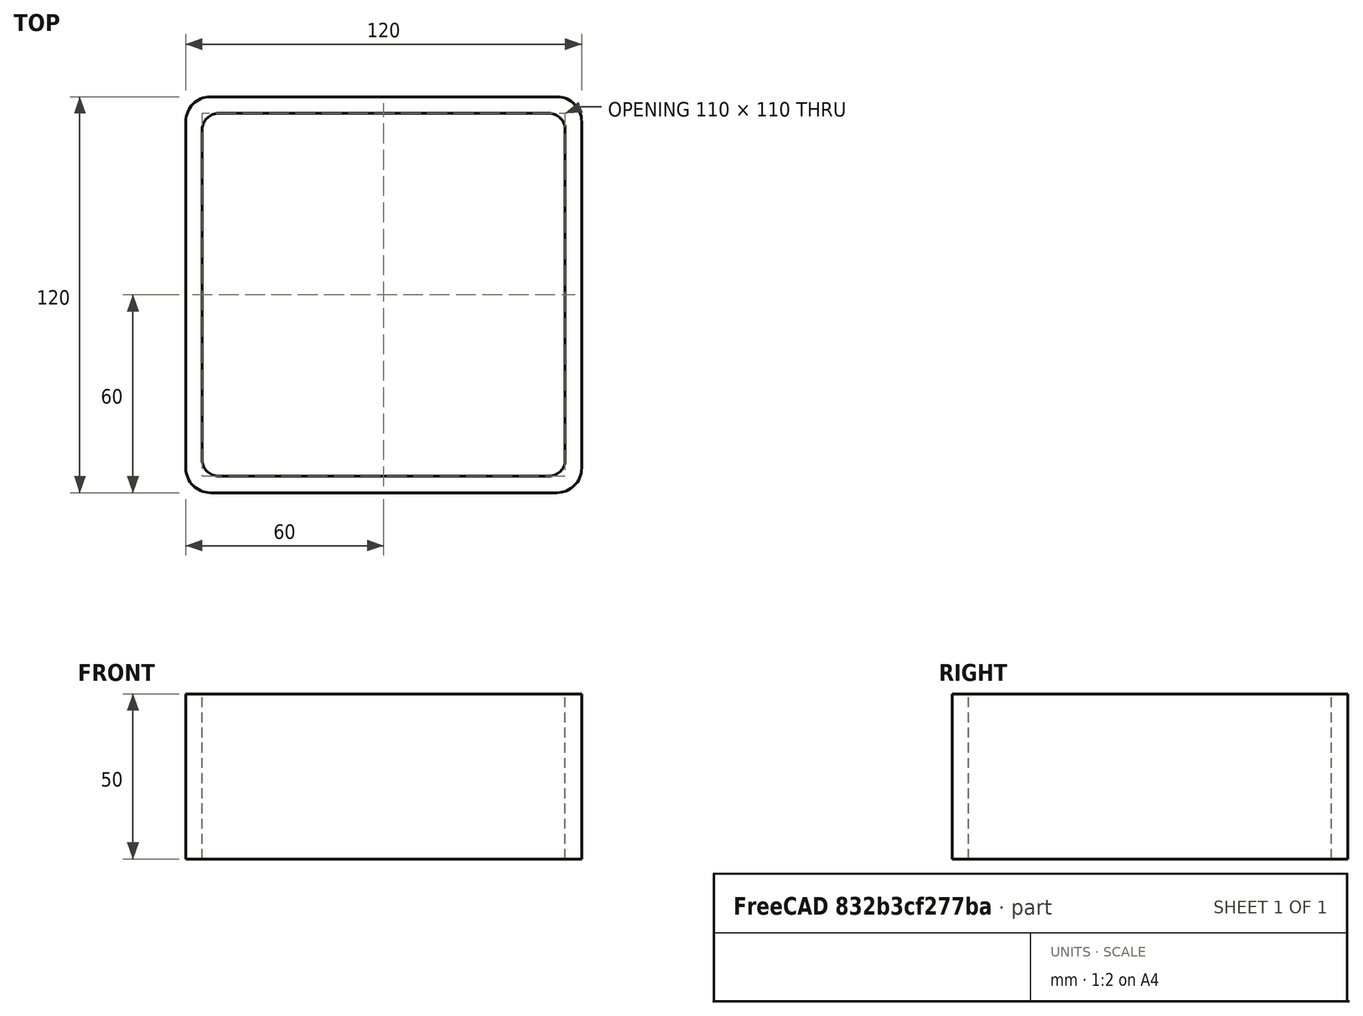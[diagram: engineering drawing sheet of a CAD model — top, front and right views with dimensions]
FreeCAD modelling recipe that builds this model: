
FCSTD DOCUMENT  (FreeCAD 0.15R4671 (Git))
Label: Square hollow section 120x120x5 EN10219 S235JRH
License: All rights reserved
LicenseURL: http://en.wikipedia.org/wiki/All_rights_reserved
objects: Sketcher::SketchObject×1, Part::Extrusion×1
note: 2 computed .brp shape members not serialized (recipe doc carries the construction recipe); baked Part::Feature solids carry a one-line shape summary decoded from their .brp

FEATURE [Sketcher::SketchObject] Sketch
  sketch-geometry (16):
    g0: LineSegment StartX=-50 StartY=55 StartZ=0 EndX=50 EndY=55 EndZ=0
    g1: LineSegment StartX=55 StartY=50 StartZ=0 EndX=55 EndY=-50 EndZ=0
    g2: LineSegment StartX=50 StartY=-55 StartZ=0 EndX=-50 EndY=-55 EndZ=0
    g3: LineSegment StartX=-55 StartY=-50 StartZ=0 EndX=-55 EndY=50 EndZ=0
    g4: LineSegment StartX=-52.5 StartY=60 StartZ=0 EndX=52.5 EndY=60 EndZ=0
    g5: LineSegment StartX=60 StartY=52.5 StartZ=0 EndX=60 EndY=-52.5 EndZ=0
    g6: LineSegment StartX=52.5 StartY=-60 StartZ=0 EndX=-52.5 EndY=-60 EndZ=0
    g7: LineSegment StartX=-60 StartY=-52.5 StartZ=0 EndX=-60 EndY=52.5 EndZ=0
    g8: ArcOfCircle CenterX=-50 CenterY=50 CenterZ=0 NormalX=0 NormalY=0 NormalZ=1 Radius=5 StartAngle=1.5708 EndAngle=3.14159
    g9: ArcOfCircle CenterX=50 CenterY=50 CenterZ=0 NormalX=0 NormalY=0 NormalZ=1 Radius=5 StartAngle=0 EndAngle=1.5708
    g10: ArcOfCircle CenterX=50 CenterY=-50 CenterZ=0 NormalX=0 NormalY=0 NormalZ=1 Radius=5 StartAngle=4.71239 EndAngle=6.28319
    g11: ArcOfCircle CenterX=-50 CenterY=-50 CenterZ=0 NormalX=0 NormalY=0 NormalZ=1 Radius=5 StartAngle=3.14159 EndAngle=4.71239
    g12: ArcOfCircle CenterX=52.5 CenterY=52.5 CenterZ=0 NormalX=0 NormalY=0 NormalZ=1 Radius=7.5 StartAngle=0 EndAngle=1.5708
    g13: ArcOfCircle CenterX=52.5 CenterY=-52.5 CenterZ=0 NormalX=0 NormalY=0 NormalZ=1 Radius=7.5 StartAngle=4.71239 EndAngle=6.28319
    g14: ArcOfCircle CenterX=-52.5 CenterY=-52.5 CenterZ=0 NormalX=0 NormalY=0 NormalZ=1 Radius=7.5 StartAngle=3.14159 EndAngle=4.71239
    g15: ArcOfCircle CenterX=-52.5 CenterY=52.5 CenterZ=0 NormalX=0 NormalY=0 NormalZ=1 Radius=7.5 StartAngle=1.5708 EndAngle=3.14159
  constraints (36):
    c: Horizontal(g2)
    c: Vertical(g3)
    c: Horizontal(g6)
    c: Vertical(g7)
    c: Tangent(g3,g8) = 1.5708
    c: Tangent(g0,g8) = 1.5708
    c: Tangent(g0,g9) = 1.5708
    c: Tangent(g1,g9) = 1.5708
    c: Tangent(g1,g10) = 1.5708
    c: Tangent(g2,g10) = 1.5708
    c: Tangent(g2,g11) = 1.5708
    c: Tangent(g3,g11) = 1.5708
    c: Tangent(g4,g12) = 1.5708
    c: Tangent(g5,g12) = 1.5708
    c: Tangent(g5,g13) = 1.5708
    c: Tangent(g6,g13) = 1.5708
    c: Tangent(g6,g14) = 1.5708
    c: Tangent(g7,g14) = 1.5708
    c: Tangent(g7,g15) = 1.5708
    c: Tangent(g4,g15) = 1.5708
    c: Equal(g9,g8)
    c: Equal(g9,g11)
    c: Equal(g9,g10)
    c: Equal(g12,g15)
    c: Equal(g12,g14)
    c: Equal(g12,g13)
    c: Symmetric(g4,g6,g-1)
    c: Symmetric(g7,g5,g-2)
    c: DistanceY(g4,g6) = -120
    c: DistanceX(g7,g5) = 120
    c: Symmetric(g3,g1,g-2)
    c: Symmetric(g0,g2,g-1)
    c: DistanceY(g0,g4) = 5
    c: DistanceX(g5,g1) = -5
    c: Radius(g9) = 5
    c: Radius(g12) = 7.5
FEATURE [Part::Extrusion] Extrude  label="Square hollow section 120x120x5 EN10219 S235JRH"
  Base = -> Sketch
  Dir = (0,0,50)
  Solid = true
